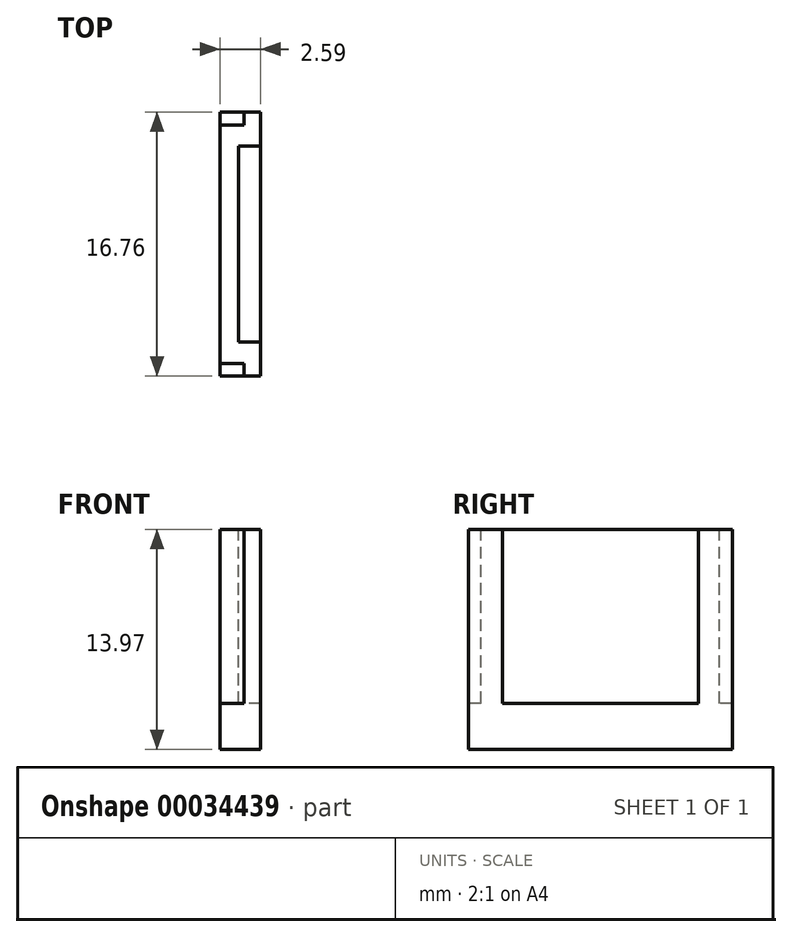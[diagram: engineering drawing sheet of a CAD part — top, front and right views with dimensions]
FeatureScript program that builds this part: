
annotation { "Feature Type Name" : "Feature", "Feature Type Description" : "" }
export const myFeature = defineFeature(function(context is Context, id is Id, definition is map)
    precondition{}
    {
        {
            var Q0;
            Q0=qCreatedBy(makeId("Front.planeOp"),FACE);
            var sketch = newSketch(context, id + "F0", { "sketchPlane" : qUnion([Q0])});
            skLineSegment(sketch, "E0.bottom", {"start": v(0, 0) * mm, "end": v(16.76, 0) * mm});
            skLineSegment(sketch, "E0.top", {"start": v(0, 2.6) * mm, "end": v(16.76, 2.6) * mm});
            skLineSegment(sketch, "E0.left", {"start": v(0, 0) * mm, "end": v(0, 2.6) * mm});
            skLineSegment(sketch, "E0.right", {"start": v(16.76, 0) * mm, "end": v(16.76, 2.6) * mm});
            skSolve(sketch);
        }
        {
            var Q0;
            Q0=makeQuery(id+"F0.imprint","IMPRINT",FACE,{"disambiguationData":[TD([[makeQuery(id+"F0.imprint","IMPRINT",EDGE,{"derivedFrom":sQuery(id+"F0.wireOp",EDGE,"E0.bottom")}),1.0]])]});
            extrude(context, id + "F1", {"entities" : qUnion([Q0]), "depth" : 13.97 * mm});
        }
        {
            var Q0;
            Q0=makeQuery(id+"F1.opExtrude","CAP_FACE",FACE,{"disambiguationData":[OSD([sQuery(id+"F0.wireOp",EDGE,"E0.bottom"),sQuery(id+"F0.wireOp",EDGE,"E0.top"),sQuery(id+"F0.wireOp",EDGE,"E0.left"),sQuery(id+"F0.wireOp",EDGE,"E0.right")])],"isStart":true});
            var sketch = newSketch(context, id + "F2", { "sketchPlane" : qUnion([Q0])});
            skLineSegment(sketch, "E1", {"start": v(-8.38, 2.6) * mm, "end": v(-8.38, 0) * mm, "construction": true});
            skLineSegment(sketch, "E2.bottom", {"start": v(-16.76, 2.6) * mm, "end": v(-15.95, 2.6) * mm});
            skLineSegment(sketch, "E2.top", {"start": v(-16.76, 1.07) * mm, "end": v(-15.95, 1.07) * mm});
            skLineSegment(sketch, "E2.left", {"start": v(-16.76, 2.6) * mm, "end": v(-16.76, 1.07) * mm});
            skLineSegment(sketch, "E2.right", {"start": v(-15.95, 2.6) * mm, "end": v(-15.95, 1.07) * mm});
            skLineSegment(sketch, "E3.MirrorCS", {"start": v(-0.81, 2.6) * mm, "end": v(-0.81, 1.07) * mm});
            skLineSegment(sketch, "E4.MirrorCS", {"start": v(0, 2.6) * mm, "end": v(0, 1.07) * mm});
            skLineSegment(sketch, "E5.MirrorCS", {"start": v(0, 1.07) * mm, "end": v(-0.81, 1.07) * mm});
            skLineSegment(sketch, "E6.MirrorCS", {"start": v(0, 2.6) * mm, "end": v(-0.81, 2.6) * mm});
            skLineSegment(sketch, "E7.bottom", {"start": v(-14.6, 0) * mm, "end": v(-2.16, 0) * mm});
            skLineSegment(sketch, "E7.top", {"start": v(-14.6, 1.4) * mm, "end": v(-2.16, 1.4) * mm});
            skLineSegment(sketch, "E7.left", {"start": v(-14.6, 0) * mm, "end": v(-14.6, 1.4) * mm});
            skLineSegment(sketch, "E7.right", {"start": v(-2.16, 0) * mm, "end": v(-2.16, 1.4) * mm});
            skSolve(sketch);
        }
        {
            var Q0;
            Q0=qSketchRegion(id+"F2",true);
            extrude(context, id + "F3", {"entities" : qUnion([Q0]), "operationType" : NewBodyOperationType.REMOVE, "oppositeDirection" : true, "depth" : 11.05 * mm});
        }
        {
            var Q0;
            Q0=makeQuery(id+"F1.opExtrude","SWEPT_BODY",BODY,{"disambiguationData":[OSD([sQuery(id+"F0.wireOp",EDGE,"E0.bottom"),sQuery(id+"F0.wireOp",EDGE,"E0.top"),sQuery(id+"F0.wireOp",EDGE,"E0.left"),sQuery(id+"F0.wireOp",EDGE,"E0.right")])]});
            var Q1;
            Q1=makeQuery(id+"F1.opExtrude","CAP_EDGE",EDGE,{"disambiguationData":[OSD([sQuery(id+"F0.wireOp",EDGE,"E0.left")])],"isStart":false});
            transform(context, id + "F4", {"entities" : qUnion([Q0]), "transformType" : TransformType.ROTATION, "transformAxis" : qUnion([Q1]), "angle" : 90 * degree, "oppositeDirection" : true, "makeCopy" : false});
        }
        {
            var Q0;
            Q0=makeQuery(id+"F1.opExtrude","SWEPT_BODY",BODY,{"disambiguationData":[OSD([sQuery(id+"F0.wireOp",EDGE,"E0.bottom"),sQuery(id+"F0.wireOp",EDGE,"E0.top"),sQuery(id+"F0.wireOp",EDGE,"E0.left"),sQuery(id+"F0.wireOp",EDGE,"E0.right")])]});
            var Q1;
            Q1=makeQuery(id+"F1.opExtrude","CAP_EDGE",EDGE,{"disambiguationData":[OSD([sQuery(id+"F0.wireOp",EDGE,"E0.bottom")])],"isStart":false});
            var Q2;
            Q2=makeQuery(id+"F1.opExtrude","CAP_EDGE",EDGE,{"disambiguationData":[OSD([sQuery(id+"F0.wireOp",EDGE,"E0.bottom")])],"isStart":false});
            transform(context, id + "F5", {"entities" : qUnion([Q0]), "transformType" : TransformType.ROTATION, "transformAxis" : qUnion([Q2]), "angle" : 90 * degree, "makeCopy" : false});
        }
    });
